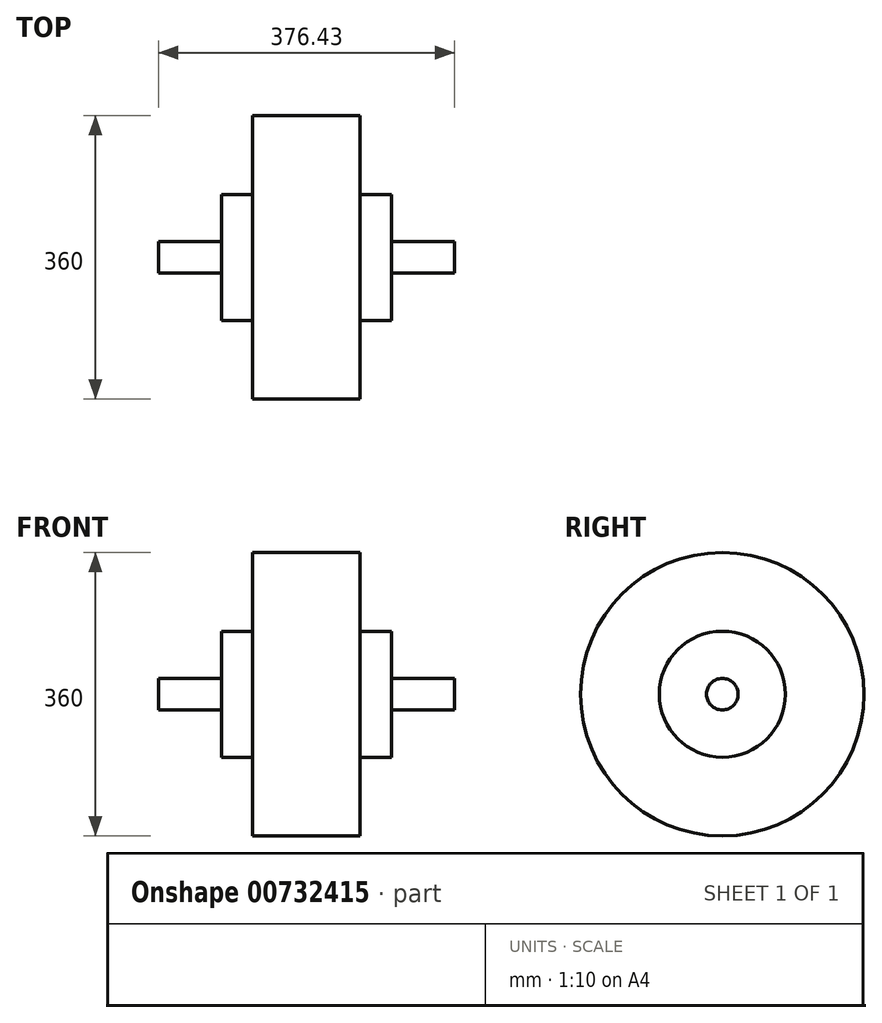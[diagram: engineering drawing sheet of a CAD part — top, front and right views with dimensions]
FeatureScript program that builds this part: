
annotation { "Feature Type Name" : "Feature", "Feature Type Description" : "" }
export const myFeature = defineFeature(function(context is Context, id is Id, definition is map)
    precondition{}
    {
        {
            var Q0;
            Q0=qCreatedBy(makeId("Front.planeOp"),FACE);
            var sketch = newSketch(context, id + "F0", { "sketchPlane" : qUnion([Q0])});
            skLineSegment(sketch, "E0", {"start": v(-376.43, 0) * mm, "end": v(-296.43, 0) * mm});
            skLineSegment(sketch, "E1", {"start": v(-296.43, 0) * mm, "end": v(-296.43, 60) * mm});
            skLineSegment(sketch, "E2", {"start": v(-296.43, 60) * mm, "end": v(-256.43, 60) * mm});
            skLineSegment(sketch, "E3", {"start": v(-256.43, 60) * mm, "end": v(-256.43, 160) * mm});
            skLineSegment(sketch, "E4", {"start": v(-256.43, 160) * mm, "end": v(-120, 160) * mm});
            skLineSegment(sketch, "E5", {"start": v(-120, 160) * mm, "end": v(-120, 60) * mm});
            skLineSegment(sketch, "E6", {"start": v(-120, 60) * mm, "end": v(-80, 60) * mm});
            skLineSegment(sketch, "E7", {"start": v(-80, 60) * mm, "end": v(-80, 0) * mm});
            skLineSegment(sketch, "E8", {"start": v(-80, 0) * mm, "end": v(0, 0) * mm});
            skLineSegment(sketch, "E9", {"start": v(0, 0) * mm, "end": v(0, -20) * mm});
            skLineSegment(sketch, "E10", {"start": v(-376.43, 0) * mm, "end": v(-376.43, -20) * mm});
            skLineSegment(sketch, "E11", {"start": v(0, -20) * mm, "end": v(-376.43, -20) * mm});
            skSolve(sketch);
        }
        {
            var Q0;
            Q0=makeQuery(id+"F0.imprint","IMPRINT",FACE,{"disambiguationData":[TD([[makeQuery(id+"F0.imprint","IMPRINT",EDGE,{"derivedFrom":sQuery(id+"F0.wireOp",EDGE,"E0")}),-1.0]])]});
            var Q1;
            Q1=sQuery(id+"F0.wireOp",EDGE,"E11");
            revolve(context, id + "F1", {"surfaceOperationType" : NewSurfaceOperationType.NEW, "entities" : qUnion([Q0]), "axis" : qUnion([Q1]), "revolveType" : RevolveType.FULL});
        }
    });
